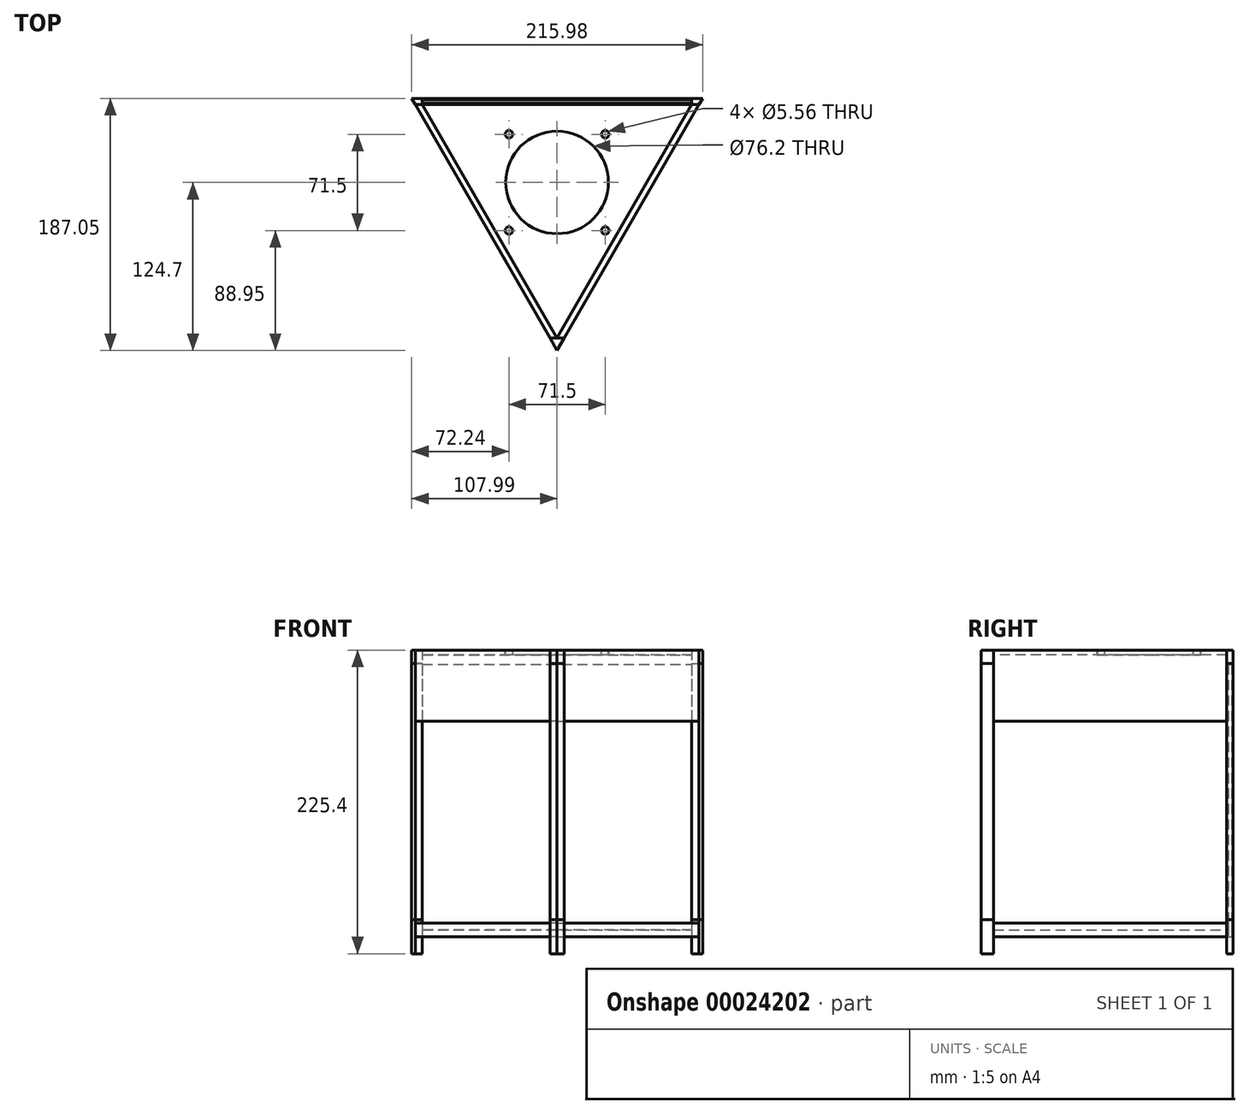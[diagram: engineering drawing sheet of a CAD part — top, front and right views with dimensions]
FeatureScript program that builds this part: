
annotation { "Feature Type Name" : "Feature", "Feature Type Description" : "" }
export const myFeature = defineFeature(function(context is Context, id is Id, definition is map)
    precondition{}
    {
        {
            var Q0;
            Q0=qCreatedBy(makeId("Top.planeOp"),FACE);
            var sketch = newSketch(context, id + "F0", { "sketchPlane" : qUnion([Q0])});
            skCircle(sketch, "E0.cCircle", {"center": v(0, 0) * mm, "radius": 115.47 * mm, "construction": true});
            skLineSegment(sketch, "E0.0", {"start": v(0, -115.47) * mm, "end": v(-100, 57.74) * mm});
            skLineSegment(sketch, "E0.1", {"start": v(-100, 57.74) * mm, "end": v(100, 57.74) * mm});
            skLineSegment(sketch, "E0.2", {"start": v(100, 57.74) * mm, "end": v(0, -115.47) * mm});
            skCircle(sketch, "E1.cCircle", {"center": v(0, 0) * mm, "radius": 124.7 * mm, "construction": true});
            skLineSegment(sketch, "E1.0", {"start": v(0, -124.7) * mm, "end": v(-108, 62.35) * mm});
            skLineSegment(sketch, "E1.1", {"start": v(-108, 62.35) * mm, "end": v(108, 62.35) * mm});
            skLineSegment(sketch, "E1.2", {"start": v(108, 62.35) * mm, "end": v(0, -124.7) * mm});
            skLineSegment(sketch, "E2", {"start": v(-100, 57.74) * mm, "end": v(-105.33, 57.74) * mm});
            skLineSegment(sketch, "E3", {"start": v(-100, 57.74) * mm, "end": v(-100, 62.35) * mm});
            skLineSegment(sketch, "E4", {"start": v(100, 57.74) * mm, "end": v(100, 62.35) * mm});
            skLineSegment(sketch, "E5", {"start": v(100, 57.74) * mm, "end": v(105.33, 57.74) * mm});
            skLineSegment(sketch, "E6", {"start": v(0, -115.47) * mm, "end": v(-5.33, -115.47) * mm});
            skLineSegment(sketch, "E7", {"start": v(0, -115.47) * mm, "end": v(5.33, -115.47) * mm});
            skLineSegment(sketch, "E8.rect.bottom", {"start": v(-100, 58.9) * mm, "end": v(100, 58.9) * mm});
            skLineSegment(sketch, "E8.rect.top", {"start": v(-100, 61.48) * mm, "end": v(100, 61.48) * mm});
            skLineSegment(sketch, "E8.rect.left", {"start": v(-100, 58.9) * mm, "end": v(-100, 61.48) * mm});
            skLineSegment(sketch, "E8.rect.right", {"start": v(100, 58.9) * mm, "end": v(100, 61.48) * mm});
            skPoint(sketch, "E8.rect.middle", {"position": v(0, 60.2) * mm});
            skSolve(sketch);
        }
        {
            var Q0;
            Q0=makeQuery(id+"F0.imprint","IMPRINT",FACE,{"disambiguationData":[TD([[makeQuery(id+"F0.imprint","IMPRINT",EDGE,{"derivedFrom":sQuery(id+"F0.wireOp",EDGE,"E0.0")}),-1.0]])]});
            extrude(context, id + "F1", {"entities" : qUnion([Q0]), "depth" : 5 * mm});
        }
        {
            var Q0;
            {var subQ1=sQuery(id+"F0.wireOp",EDGE,"E2");Q0=makeQuery(id+"F0.imprint","IMPRINT",FACE,{"disambiguationData":[TD([[makeQuery(id+"F0.imprint","IMPRINT",EDGE,{"derivedFrom":subQ1}),-1.0]])]});}
            var Q1;
            {var subQ1=sQuery(id+"F0.wireOp",EDGE,"E6");Q1=makeQuery(id+"F0.imprint","IMPRINT",FACE,{"disambiguationData":[TD([[makeQuery(id+"F0.imprint","IMPRINT",EDGE,{"derivedFrom":subQ1}),1.0]])]});}
            var Q2;
            {var subQ0=sQuery(id+"F0.wireOp",EDGE,"E4");Q2=makeQuery(id+"F0.imprint","IMPRINT",FACE,{"disambiguationData":[TD([[makeQuery(id+"F0.imprint","IMPRINT",EDGE,{"derivedFrom":subQ0}),-1.0]])]});}
            extrude(context, id + "F2", {"entities" : qUnion([Q0, Q1, Q2]), "endBound" : BoundingType.SYMMETRIC, "depth" : 25.4 * mm});
        }
        {
            var Q0;
            Q0=makeQuery(id+"F2.opExtrude","CAP_FACE",FACE,{"disambiguationData":[OSD([sQuery(id+"F0.wireOp",EDGE,"E1.0"),sQuery(id+"F0.wireOp",EDGE,"E1.1"),sQuery(id+"F0.wireOp",EDGE,"E2"),sQuery(id+"F0.wireOp",EDGE,"E3")])],"isStart":false});
            var Q1;
            Q1=makeQuery(id+"F2.opExtrude","CAP_FACE",FACE,{"disambiguationData":[OSD([sQuery(id+"F0.wireOp",EDGE,"E1.1"),sQuery(id+"F0.wireOp",EDGE,"E1.2"),sQuery(id+"F0.wireOp",EDGE,"E4"),sQuery(id+"F0.wireOp",EDGE,"E5")])],"isStart":false});
            var Q2;
            Q2=makeQuery(id+"F2.opExtrude","CAP_FACE",FACE,{"disambiguationData":[OSD([sQuery(id+"F0.wireOp",EDGE,"E1.0"),sQuery(id+"F0.wireOp",EDGE,"E1.2"),sQuery(id+"F0.wireOp",EDGE,"E6"),sQuery(id+"F0.wireOp",EDGE,"E7")])],"isStart":false});
            extrude(context, id + "F3", {"entities" : qUnion([Q0, Q1, Q2]), "depth" : 190 * mm});
        }
        {
            var Q0;
            {var subQ2=sQuery(id+"F0.wireOp",EDGE,"E0.1");Q0=makeQuery(id+"F0.imprint","IMPRINT",FACE,{"disambiguationData":[TD([[makeQuery(id+"F0.imprint","IMPRINT",EDGE,{"derivedFrom":subQ2}),1.0]])]});}
            var Q1;
            {var subQ1=sQuery(id+"F0.wireOp",EDGE,"E8.rect.top");Q1=makeQuery(id+"F0.imprint","IMPRINT",FACE,{"disambiguationData":[TD([[makeQuery(id+"F0.imprint","IMPRINT",EDGE,{"derivedFrom":subQ1}),1.0]])]});}
            extrude(context, id + "F4", {"entities" : qUnion([Q0, Q1]), "depth" : 10 * mm});
        }
        {
            var Q0;
            Q0=makeQuery(id+"F0.imprint","IMPRINT",FACE,{"disambiguationData":[TD([[makeQuery(id+"F0.imprint","IMPRINT",EDGE,{"derivedFrom":sQuery(id+"F0.wireOp",EDGE,"E8.rect.bottom")}),1.0]])]});
            extrude(context, id + "F5", {"entities" : qUnion([Q0]), "depth" : 202 * mm});
        }
        {
            var Q0;
            Q0=makeQuery(id+"F0.imprint","IMPRINT",FACE,{"disambiguationData":[TD([[makeQuery(id+"F0.imprint","IMPRINT",EDGE,{"derivedFrom":sQuery(id+"F0.wireOp",EDGE,"E0.0")}),1.0]])]});
            extrude(context, id + "F6", {"entities" : qUnion([Q0]), "depth" : 10 * mm});
        }
        {
            var Q0;
            Q0=makeQuery(id+"F0.imprint","IMPRINT",FACE,{"disambiguationData":[TD([[makeQuery(id+"F0.imprint","IMPRINT",EDGE,{"derivedFrom":sQuery(id+"F0.wireOp",EDGE,"E0.2")}),1.0]])]});
            extrude(context, id + "F7", {"entities" : qUnion([Q0]), "depth" : 10 * mm});
        }
        {
            var Q0;
            Q0=makeQuery(id+"F3.opExtrude","CAP_FACE",FACE,{"disambiguationData":[OSD([sQuery(id+"F0.wireOp",EDGE,"E1.0"),sQuery(id+"F0.wireOp",EDGE,"E1.2"),sQuery(id+"F0.wireOp",EDGE,"E6"),sQuery(id+"F0.wireOp",EDGE,"E7")])],"isStart":false});
            var Q1;
            Q1=makeQuery(id+"F3.opExtrude","CAP_FACE",FACE,{"disambiguationData":[OSD([sQuery(id+"F0.wireOp",EDGE,"E1.0"),sQuery(id+"F0.wireOp",EDGE,"E1.1"),sQuery(id+"F0.wireOp",EDGE,"E2"),sQuery(id+"F0.wireOp",EDGE,"E3"),sQuery(id+"F0.wireOp",EDGE,"E8.rect.left")])],"isStart":false});
            var Q2;
            Q2=makeQuery(id+"F3.opExtrude","CAP_FACE",FACE,{"disambiguationData":[OSD([sQuery(id+"F0.wireOp",EDGE,"E1.1"),sQuery(id+"F0.wireOp",EDGE,"E1.2"),sQuery(id+"F0.wireOp",EDGE,"E4"),sQuery(id+"F0.wireOp",EDGE,"E5"),sQuery(id+"F0.wireOp",EDGE,"E8.rect.right")])],"isStart":false});
            extrude(context, id + "F8", {"entities" : qUnion([Q0, Q1, Q2]), "depth" : 10 * mm});
        }
        {
            var Q0;
            Q0=makeQuery(id+"F1.opExtrude","CAP_FACE",FACE,{"disambiguationData":[OSD([sQuery(id+"F0.wireOp",EDGE,"E0.0"),sQuery(id+"F0.wireOp",EDGE,"E0.1"),sQuery(id+"F0.wireOp",EDGE,"E0.2")])],"isStart":false});
            var Q1;
            Q1=makeQuery(id+"F8.opExtrude","CAP_FACE",FACE,{"disambiguationData":[OSD([sQuery(id+"F0.wireOp",EDGE,"E1.1"),sQuery(id+"F0.wireOp",EDGE,"E1.2"),sQuery(id+"F0.wireOp",EDGE,"E4"),sQuery(id+"F0.wireOp",EDGE,"E5"),sQuery(id+"F0.wireOp",EDGE,"E8.rect.right")])],"isStart":false});
            extrude(context, id + "F9", {"entities" : qUnion([Q0]), "endBound" : BoundingType.UP_TO_SURFACE, "endBoundEntityFace" : qUnion([Q1]), "depth" : 25.4 * mm, "hasSecondDirection" : true, "secondDirectionOppositeDirection" : false, "secondDirectionDepth" : 204 * mm});
        }
        {
            var Q0;
            Q0=makeQuery(id+"F7.opExtrude","CAP_FACE",FACE,{"disambiguationData":[OSD([sQuery(id+"F0.wireOp",EDGE,"E0.2"),sQuery(id+"F0.wireOp",EDGE,"E1.2"),sQuery(id+"F0.wireOp",EDGE,"E5"),sQuery(id+"F0.wireOp",EDGE,"E7")])],"isStart":false});
            var Q1;
            Q1=makeQuery(id+"F6.opExtrude","CAP_FACE",FACE,{"disambiguationData":[OSD([sQuery(id+"F0.wireOp",EDGE,"E0.0"),sQuery(id+"F0.wireOp",EDGE,"E1.0"),sQuery(id+"F0.wireOp",EDGE,"E2"),sQuery(id+"F0.wireOp",EDGE,"E6")])],"isStart":false});
            var Q2;
            Q2=makeQuery(id+"F8.opExtrude","CAP_FACE",FACE,{"disambiguationData":[OSD([sQuery(id+"F0.wireOp",EDGE,"E1.0"),sQuery(id+"F0.wireOp",EDGE,"E1.2"),sQuery(id+"F0.wireOp",EDGE,"E6"),sQuery(id+"F0.wireOp",EDGE,"E7")])],"isStart":false});
            extrude(context, id + "F10", {"entities" : qUnion([Q0, Q1]), "endBound" : BoundingType.UP_TO_SURFACE, "endBoundEntityFace" : qUnion([Q2]), "depth" : 205 * mm, "hasSecondDirection" : true, "secondDirectionOppositeDirection" : false, "secondDirectionDepth" : 150 * mm});
        }
        {
            var Q0;
            Q0=makeQuery(id+"F9.opExtrude","CAP_FACE",FACE,{"disambiguationData":[OSD([sQuery(id+"F0.wireOp",EDGE,"E0.0"),sQuery(id+"F0.wireOp",EDGE,"E0.1"),sQuery(id+"F0.wireOp",EDGE,"E0.2")])],"isStart":false});
            var sketch = newSketch(context, id + "F11", { "sketchPlane" : qUnion([Q0])});
            skLineSegment(sketch, "E9.rect.bottom", {"start": v(40, 40) * mm, "end": v(-40, 40) * mm});
            skLineSegment(sketch, "E9.rect.top", {"start": v(40, -40) * mm, "end": v(-40, -40) * mm});
            skLineSegment(sketch, "E9.rect.left", {"start": v(40, 40) * mm, "end": v(40, -40) * mm});
            skLineSegment(sketch, "E9.rect.right", {"start": v(-40, 40) * mm, "end": v(-40, -40) * mm});
            skPoint(sketch, "E9.rect.middle", {"position": v(0, 0) * mm});
            skCircle(sketch, "E10", {"center": v(-35.75, 35.75) * mm, "radius": 2.78 * mm});
            skCircle(sketch, "E11", {"center": v(35.75, 35.75) * mm, "radius": 2.78 * mm});
            skCircle(sketch, "E12", {"center": v(35.75, -35.75) * mm, "radius": 2.78 * mm});
            skCircle(sketch, "E13", {"center": v(-35.75, -35.75) * mm, "radius": 2.78 * mm});
            skCircle(sketch, "E14", {"center": v(0, 0) * mm, "radius": 37.5 * mm});
            skSolve(sketch);
        }
        {
            var Q0;
            Q0=sQuery(id+"F11.wireOp",VERTEX,"E9.rect.middle");
            var Q1;
            Q1=makeQuery(id+"F9.opExtrude","SWEPT_BODY",BODY,{"disambiguationData":[OSD([sQuery(id+"F0.wireOp",EDGE,"E0.0"),sQuery(id+"F0.wireOp",EDGE,"E0.1"),sQuery(id+"F0.wireOp",EDGE,"E0.2")])]});
            hole(context, id + "F12", {"style" : HoleStyle.SIMPLE, "holeDiameter" : 76.2 * mm, "endStyle" : HoleEndStyle.THROUGH, "locations" : qUnion([Q0]), "scope" : qUnion([Q1])});
        }
        {
            var Q0;
            Q0=sQuery(id+"F11.wireOp",VERTEX,"E10.center");
            var Q1;
            Q1=sQuery(id+"F11.wireOp",VERTEX,"E11.center");
            var Q2;
            Q2=sQuery(id+"F11.wireOp",VERTEX,"E12.center");
            var Q3;
            Q3=sQuery(id+"F11.wireOp",VERTEX,"E13.center");
            var Q4;
            Q4=makeQuery(id+"F9.opExtrude","SWEPT_BODY",BODY,{"disambiguationData":[OSD([sQuery(id+"F0.wireOp",EDGE,"E0.0"),sQuery(id+"F0.wireOp",EDGE,"E0.1"),sQuery(id+"F0.wireOp",EDGE,"E0.2")])]});
            hole(context, id + "F13", {"style" : HoleStyle.SIMPLE, "holeDiameter" : 5.56 * mm, "endStyle" : HoleEndStyle.THROUGH, "locations" : qUnion([Q0, Q1, Q2, Q3]), "scope" : qUnion([Q4])});
        }
    });
